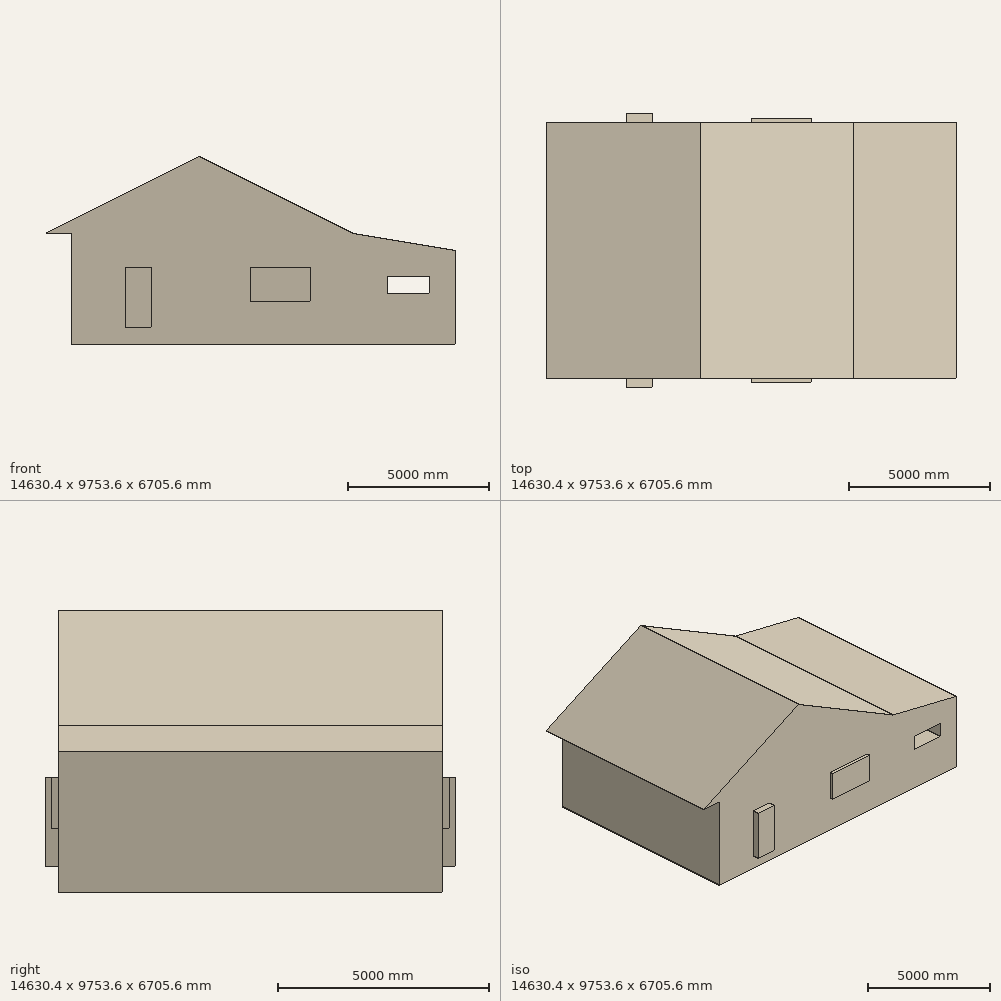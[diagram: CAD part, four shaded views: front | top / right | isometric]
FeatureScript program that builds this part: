
annotation { "Feature Type Name" : "Feature", "Feature Type Description" : "" }
export const myFeature = defineFeature(function(context is Context, id is Id, definition is map)
    precondition{}
    {
        {
            var Q0;
            Q0=qCreatedBy(makeId("Front.planeOp"),FACE);
            var sketch = newSketch(context, id + "F0", { "sketchPlane" : qUnion([Q0])});
            skLineSegment(sketch, "E0", {"start": v(0, 0) * mm, "end": v(-4572, 0) * mm});
            skLineSegment(sketch, "E1", {"start": v(0, 0) * mm, "end": v(4572, 0) * mm});
            skLineSegment(sketch, "E2", {"start": v(0, 0) * mm, "end": v(0, 2286) * mm});
            skLineSegment(sketch, "E3", {"start": v(0, 2286) * mm, "end": v(-4572, 0) * mm});
            skLineSegment(sketch, "E4", {"start": v(0, 2286) * mm, "end": v(4572, 0) * mm});
            skLineSegment(sketch, "E5", {"start": v(-4572, 0) * mm, "end": v(-5486.4, 0) * mm});
            skLineSegment(sketch, "E6", {"start": v(0, 2286) * mm, "end": v(0, 2743.2) * mm});
            skLineSegment(sketch, "E7", {"start": v(0, 2743.2) * mm, "end": v(-5486.4, 0) * mm});
            skLineSegment(sketch, "E8", {"start": v(4572, 0) * mm, "end": v(5486.4, 0) * mm});
            skLineSegment(sketch, "E9", {"start": v(0, 2743.2) * mm, "end": v(5486.4, 0) * mm});
            skLineSegment(sketch, "E10", {"start": v(-4572, 0) * mm, "end": v(-4572, -3352.8) * mm});
            skLineSegment(sketch, "E11", {"start": v(4572, 0) * mm, "end": v(4572, -3352.8) * mm});
            skLineSegment(sketch, "E12", {"start": v(4572, -3352.8) * mm, "end": v(-4572, -3352.8) * mm});
            skLineSegment(sketch, "E13", {"start": v(4572, -3352.8) * mm, "end": v(9144, -3352.8) * mm});
            skLineSegment(sketch, "E14", {"start": v(9144, -3352.8) * mm, "end": v(9144, -609.6) * mm});
            skLineSegment(sketch, "E15", {"start": v(5486.4, 0) * mm, "end": v(9144, -609.6) * mm});
            skLineSegment(sketch, "E16", {"start": v(-4572, -3352.8) * mm, "end": v(-4572, -3962.4) * mm});
            skLineSegment(sketch, "E17", {"start": v(9144, -3352.8) * mm, "end": v(9144, -3962.4) * mm});
            skLineSegment(sketch, "E18", {"start": v(-4572, -3962.4) * mm, "end": v(9144, -3962.4) * mm});
            skLineSegment(sketch, "E19.bottom", {"start": v(1828.8, -1219.2) * mm, "end": v(3962.4, -1219.2) * mm});
            skLineSegment(sketch, "E19.top", {"start": v(1828.8, -2438.4) * mm, "end": v(3962.4, -2438.4) * mm});
            skLineSegment(sketch, "E19.left", {"start": v(1828.8, -1219.2) * mm, "end": v(1828.8, -2438.4) * mm});
            skLineSegment(sketch, "E19.right", {"start": v(3962.4, -1219.2) * mm, "end": v(3962.4, -2438.4) * mm});
            skLineSegment(sketch, "E20.bottom", {"start": v(6705.6, -1524) * mm, "end": v(8229.6, -1524) * mm});
            skLineSegment(sketch, "E20.top", {"start": v(6705.6, -2133.6) * mm, "end": v(8229.6, -2133.6) * mm});
            skLineSegment(sketch, "E20.left", {"start": v(6705.6, -1524) * mm, "end": v(6705.6, -2133.6) * mm});
            skLineSegment(sketch, "E20.right", {"start": v(8229.6, -1524) * mm, "end": v(8229.6, -2133.6) * mm});
            skLineSegment(sketch, "E21", {"start": v(-2632.37, -3352.8) * mm, "end": v(-2632.37, -1219.2) * mm});
            skLineSegment(sketch, "E22", {"start": v(-2632.37, -1219.2) * mm, "end": v(-1717.97, -1219.2) * mm});
            skLineSegment(sketch, "E23", {"start": v(-1717.97, -1219.2) * mm, "end": v(-1717.97, -3352.8) * mm});
            skLineSegment(sketch, "E24", {"start": v(-1717.97, -3352.8) * mm, "end": v(-2632.37, -3352.8) * mm});
            skSolve(sketch);
        }
        {
            var Q0;
            Q0=makeQuery(id+"F0.imprint","IMPRINT",FACE,{"disambiguationData":[TD([[makeQuery(id+"F0.imprint","IMPRINT",EDGE,{"derivedFrom":sQuery(id+"F0.wireOp",EDGE,"E21")}),-1.0]])]});
            extrude(context, id + "F1", {"entities" : qUnion([Q0]), "endBound" : BoundingType.SYMMETRIC, "depth" : 9753.6 * mm, "offsetDistance" : 30.48 * mm});
        }
        {
            var Q0;
            Q0=makeQuery(id+"F0.imprint","IMPRINT",FACE,{"disambiguationData":[TD([[makeQuery(id+"F0.imprint","IMPRINT",EDGE,{"derivedFrom":sQuery(id+"F0.wireOp",EDGE,"E0")}),1.0]])]});
            extrude(context, id + "F2", {"entities" : qUnion([Q0]), "operationType" : NewBodyOperationType.ADD, "endBound" : BoundingType.SYMMETRIC, "depth" : 9144 * mm, "offsetDistance" : 30.48 * mm});
        }
        {
            var Q0;
            Q0=makeQuery(id+"F0.imprint","IMPRINT",FACE,{"disambiguationData":[TD([[makeQuery(id+"F0.imprint","IMPRINT",EDGE,{"derivedFrom":sQuery(id+"F0.wireOp",EDGE,"E8")}),-1.0]])]});
            extrude(context, id + "F3", {"entities" : qUnion([Q0]), "operationType" : NewBodyOperationType.ADD, "endBound" : BoundingType.SYMMETRIC, "depth" : 9144 * mm, "offsetDistance" : 30.48 * mm});
        }
        {
            var Q0;
            Q0 = qSketchRegion(id + "F0", true);
            var Q1;
            Q1=makeQuery(id+"F0.imprint","IMPRINT",FACE,{"disambiguationData":[TD([[makeQuery(id+"F0.imprint","IMPRINT",EDGE,{"derivedFrom":sQuery(id+"F0.wireOp",EDGE,"E1")}),1.0]])]});
            extrude(context, id + "F4", {"entities" : qUnion([Q0, Q1]), "operationType" : NewBodyOperationType.ADD, "endBound" : BoundingType.SYMMETRIC, "depth" : 9144 * mm, "offsetDistance" : 30.48 * mm});
        }
        {
            var Q0;
            Q0=makeQuery(id+"F0.imprint","IMPRINT",FACE,{"disambiguationData":[TD([[makeQuery(id+"F0.imprint","IMPRINT",EDGE,{"derivedFrom":sQuery(id+"F0.wireOp",EDGE,"E19.bottom")}),-1.0]])]});
            extrude(context, id + "F5", {"entities" : qUnion([Q0]), "operationType" : NewBodyOperationType.ADD, "endBound" : BoundingType.SYMMETRIC, "depth" : 9448.8 * mm, "offsetDistance" : 30.48 * mm});
        }
    });
